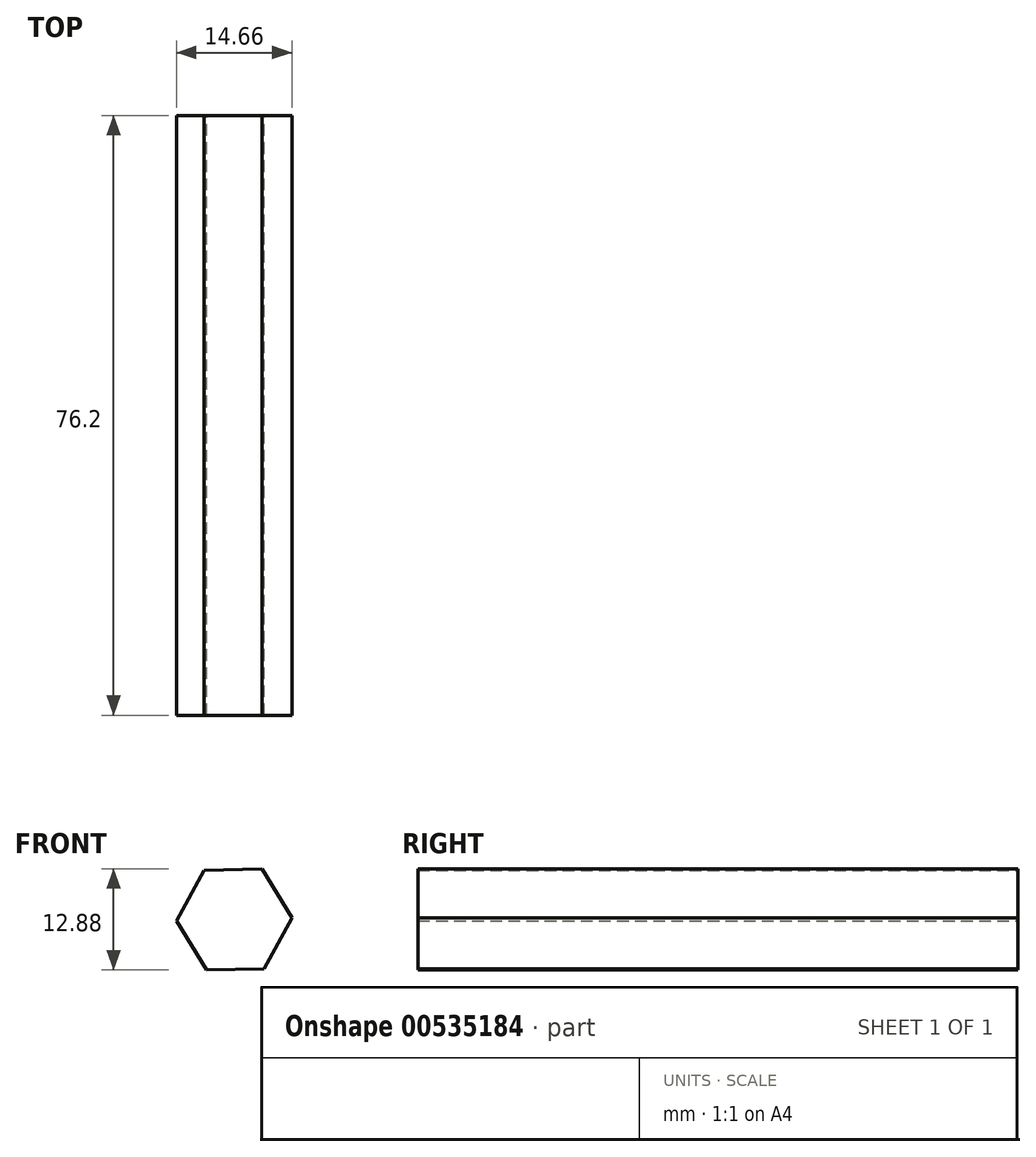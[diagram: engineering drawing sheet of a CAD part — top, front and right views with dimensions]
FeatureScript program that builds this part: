
annotation { "Feature Type Name" : "Feature", "Feature Type Description" : "" }
export const myFeature = defineFeature(function(context is Context, id is Id, definition is map)
    precondition{}
    {
        {
            var Q0;
            Q0=qCreatedBy(makeId("Front.planeOp"),FACE);
            var sketch = newSketch(context, id + "F0", { "sketchPlane" : qUnion([Q0])});
            skCircle(sketch, "E0.cCircle", {"center": v(0, 0) * mm, "radius": 6.35 * mm, "construction": true});
            skLineSegment(sketch, "E0.0", {"start": v(3.51, 6.44) * mm, "end": v(7.33, 0.18) * mm});
            skLineSegment(sketch, "E0.1", {"start": v(7.33, 0.18) * mm, "end": v(3.82, -6.26) * mm});
            skLineSegment(sketch, "E0.2", {"start": v(3.82, -6.26) * mm, "end": v(-3.51, -6.44) * mm});
            skLineSegment(sketch, "E0.3", {"start": v(-3.51, -6.44) * mm, "end": v(-7.33, -0.18) * mm});
            skLineSegment(sketch, "E0.4", {"start": v(-7.33, -0.18) * mm, "end": v(-3.82, 6.26) * mm});
            skLineSegment(sketch, "E0.5", {"start": v(-3.82, 6.26) * mm, "end": v(3.51, 6.44) * mm});
            skPoint(sketch, "E0.0.midPoint", {"position": v(5.42, 3.3) * mm});
            skSolve(sketch);
        }
        {
            var Q0;
            Q0=qSketchRegion(id+"F0",true);
            extrude(context, id + "F1", {"entities" : qUnion([Q0]), "depth" : 76.2 * mm});
        }
    });
